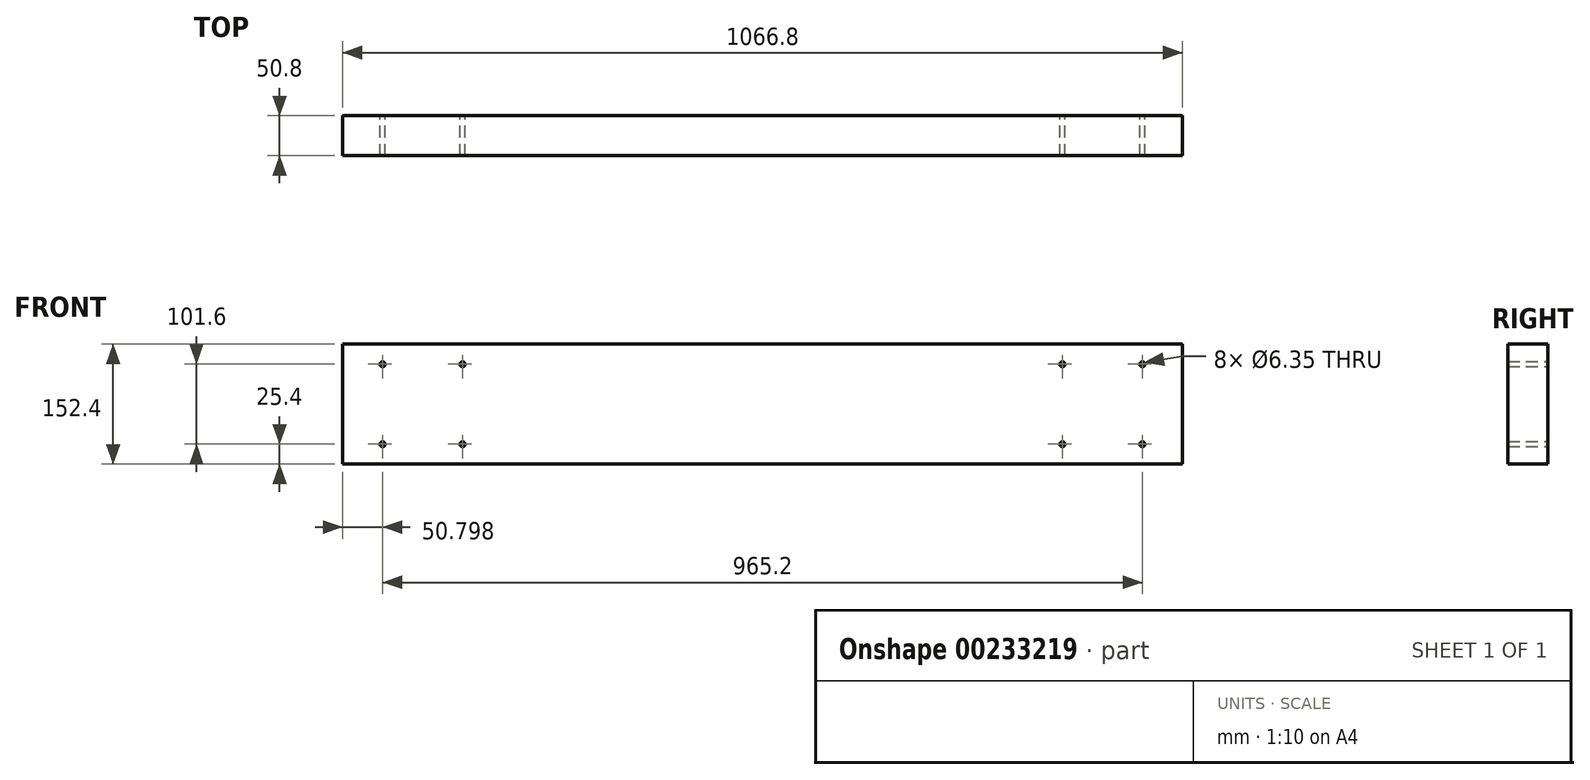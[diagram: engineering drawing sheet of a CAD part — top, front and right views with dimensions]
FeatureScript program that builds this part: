
annotation { "Feature Type Name" : "Feature", "Feature Type Description" : "" }
export const myFeature = defineFeature(function(context is Context, id is Id, definition is map)
    precondition{}
    {
        {
            var Q0;
            Q0=qCreatedBy(makeId("Front.planeOp"),FACE);
            var sketch = newSketch(context, id + "F0", { "sketchPlane" : qUnion([Q0])});
            skLineSegment(sketch, "E0.bottom", {"start": v(-114.74, 152.4) * mm, "end": v(952.06, 152.4) * mm});
            skLineSegment(sketch, "E0.top", {"start": v(-114.74, 0) * mm, "end": v(952.06, 0) * mm});
            skLineSegment(sketch, "E0.left", {"start": v(-114.74, 152.4) * mm, "end": v(-114.74, 0) * mm});
            skLineSegment(sketch, "E0.right", {"start": v(952.06, 152.4) * mm, "end": v(952.06, 0) * mm});
            skCircle(sketch, "E1", {"center": v(-63.94, 127) * mm, "radius": 3.18 * mm});
            skCircle(sketch, "E2", {"center": v(-63.94, 25.4) * mm, "radius": 3.18 * mm});
            skCircle(sketch, "E3", {"center": v(37.66, 127) * mm, "radius": 3.17 * mm});
            skCircle(sketch, "E4", {"center": v(37.66, 25.4) * mm, "radius": 3.18 * mm});
            skCircle(sketch, "E5", {"center": v(799.66, 25.4) * mm, "radius": 3.18 * mm});
            skCircle(sketch, "E6", {"center": v(799.66, 127) * mm, "radius": 3.18 * mm});
            skCircle(sketch, "E7", {"center": v(901.26, 25.4) * mm, "radius": 3.18 * mm});
            skCircle(sketch, "E8", {"center": v(901.26, 127) * mm, "radius": 3.17 * mm});
            skSolve(sketch);
        }
        {
            var Q0;
            Q0 = qSketchRegion(id + "F0", true);
            extrude(context, id + "F1", {"entities" : qUnion([Q0]), "depth" : 50.8 * mm});
        }
    });
